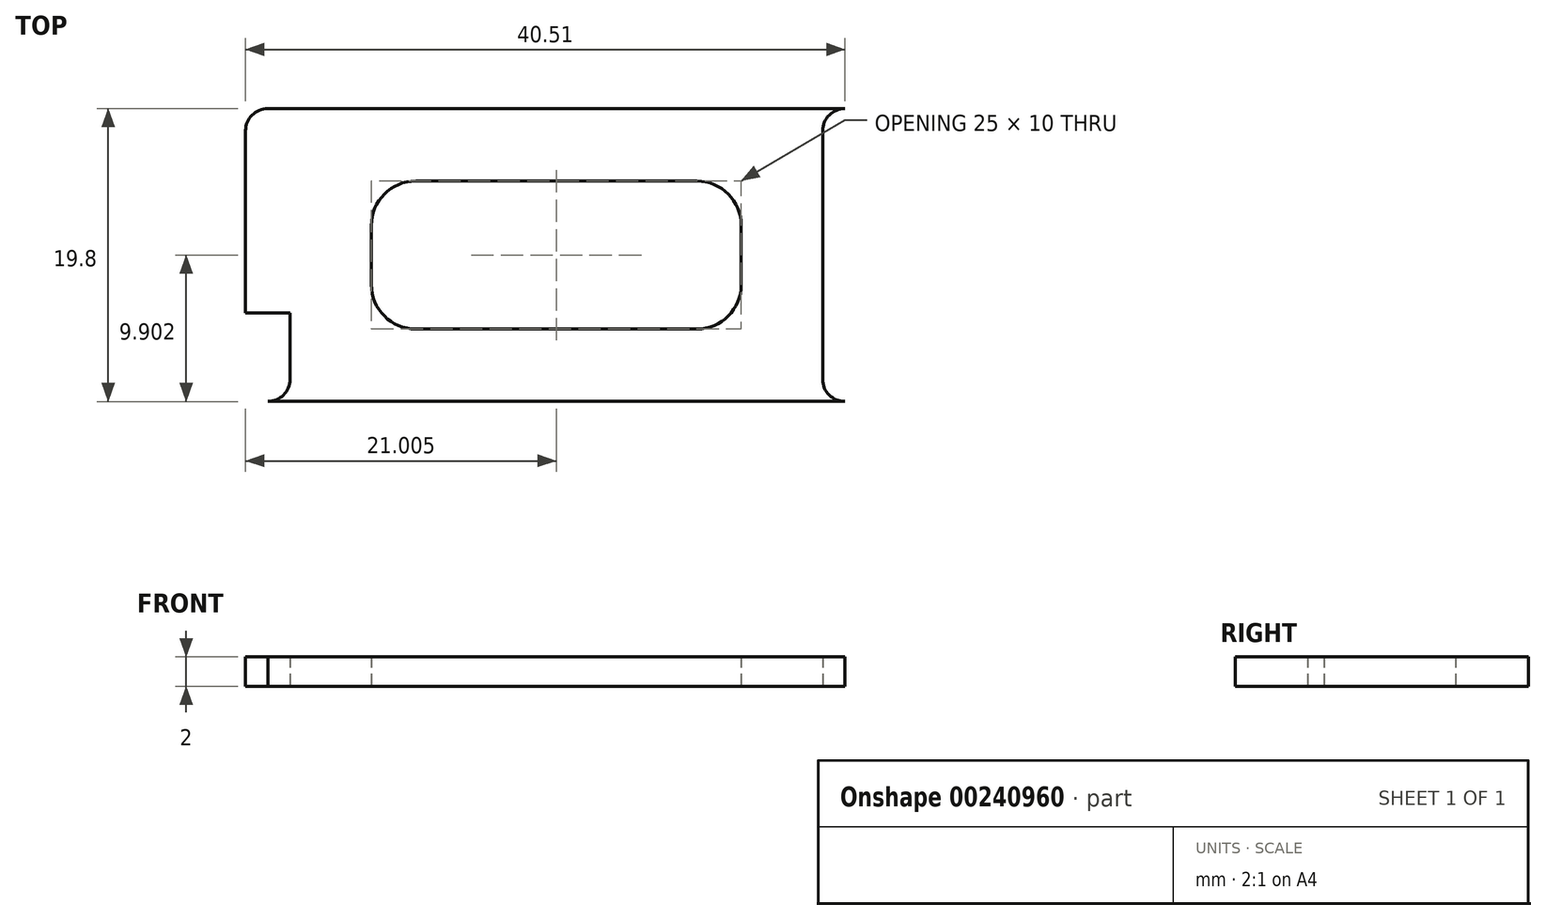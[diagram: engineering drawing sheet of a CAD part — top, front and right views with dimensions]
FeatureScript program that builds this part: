
annotation { "Feature Type Name" : "Feature", "Feature Type Description" : "" }
export const myFeature = defineFeature(function(context is Context, id is Id, definition is map)
    precondition{}
    {
        {
            var Q0;
            Q0=qCreatedBy(makeId("Top.planeOp"),FACE);
            var sketch = newSketch(context, id + "F0", { "sketchPlane" : qUnion([Q0])});
            skLineSegment(sketch, "E0.bottom", {"start": v(-18.53, 9.8) * mm, "end": v(-18.53, 9.8) * mm});
            skLineSegment(sketch, "E0.top", {"start": v(-18.53, -10) * mm, "end": v(-18.53, -10) * mm});
            skLineSegment(sketch, "E0.left", {"start": v(-20.03, 8.3) * mm, "end": v(-20.03, -8.5) * mm});
            skLineSegment(sketch, "E0.right", {"start": v(-17.03, 8.3) * mm, "end": v(-17.03, -8.5) * mm});
            skPoint(sketch, "E0.middle", {"position": v(-18.53, -0.1) * mm});
            skPoint(sketch, "E1.visualSharp", {"position": v(-20.03, 9.8) * mm});
            skArc(sketch, "E1.filletArc", {"start": v(-18.53, 9.8) * mm, "mid": v(-19.59, 9.35) * mm, "end": v(-20.03, 8.3) * mm});
            skPoint(sketch, "E2.visualSharp", {"position": v(-17.03, 9.8) * mm});
            skArc(sketch, "E2.filletArc", {"start": v(-17.03, 8.3) * mm, "mid": v(-17.46, 9.35) * mm, "end": v(-18.53, 9.8) * mm});
            skPoint(sketch, "E3.visualSharp", {"position": v(-17.03, -10) * mm});
            skArc(sketch, "E3.filletArc", {"start": v(-18.53, -10) * mm, "mid": v(-17.46, -9.57) * mm, "end": v(-17.03, -8.5) * mm});
            skPoint(sketch, "E4.visualSharp", {"position": v(-20.03, -10) * mm});
            skArc(sketch, "E4.filletArc", {"start": v(-20.03, -8.5) * mm, "mid": v(-19.59, -9.57) * mm, "end": v(-18.53, -10) * mm});
            skLineSegment(sketch, "E5", {"start": v(0.97, -11.31) * mm, "end": v(0.97, 19.7) * mm, "construction": true});
            skArc(sketch, "E6.MirrorCS", {"start": v(18.98, 8.3) * mm, "mid": v(19.41, 9.35) * mm, "end": v(20.48, 9.8) * mm});
            skArc(sketch, "E7.MirrorCS", {"start": v(20.48, -10) * mm, "mid": v(19.41, -9.57) * mm, "end": v(18.98, -8.5) * mm});
            skArc(sketch, "E8.MirrorCS", {"start": v(20.48, 9.8) * mm, "mid": v(21.54, 9.35) * mm, "end": v(21.98, 8.3) * mm});
            skArc(sketch, "E9.MirrorCS", {"start": v(21.98, -8.5) * mm, "mid": v(21.54, -9.57) * mm, "end": v(20.48, -10) * mm});
            skLineSegment(sketch, "E10.MirrorCS", {"start": v(18.97, 8.3) * mm, "end": v(18.97, -8.5) * mm});
            skLineSegment(sketch, "E11.MirrorCS", {"start": v(21.98, 8.3) * mm, "end": v(21.98, -8.5) * mm});
            skPoint(sketch, "E12.MirrorP", {"position": v(21.98, 9.8) * mm});
            skPoint(sketch, "E13.MirrorP", {"position": v(20.48, -0.1) * mm});
            skPoint(sketch, "E14.MirrorP", {"position": v(21.98, -10) * mm});
            skPoint(sketch, "E15.MirrorP", {"position": v(18.97, -10) * mm});
            skPoint(sketch, "E16.MirrorP", {"position": v(18.97, 9.8) * mm});
            skLineSegment(sketch, "E17", {"start": v(-18.53, 9.8) * mm, "end": v(20.48, 9.8) * mm});
            skLineSegment(sketch, "E18", {"start": v(-18.53, -10) * mm, "end": v(20.48, -10) * mm});
            skLineSegment(sketch, "E19.bottom", {"start": v(-8.53, 4.9) * mm, "end": v(10.47, 4.9) * mm});
            skLineSegment(sketch, "E19.top", {"start": v(-8.53, -5.1) * mm, "end": v(10.47, -5.1) * mm});
            skLineSegment(sketch, "E19.left", {"start": v(-11.53, 1.9) * mm, "end": v(-11.53, -2.1) * mm});
            skLineSegment(sketch, "E19.right", {"start": v(13.47, 1.9) * mm, "end": v(13.47, -2.1) * mm});
            skPoint(sketch, "E19.middle", {"position": v(0.97, -0.1) * mm});
            skPoint(sketch, "E20.visualSharp", {"position": v(-11.53, 4.9) * mm});
            skArc(sketch, "E20.filletArc", {"start": v(-8.53, 4.9) * mm, "mid": v(-10.65, 4.01) * mm, "end": v(-11.53, 1.9) * mm});
            skPoint(sketch, "E21.visualSharp", {"position": v(-11.53, -5.1) * mm});
            skArc(sketch, "E21.filletArc", {"start": v(-11.53, -2.1) * mm, "mid": v(-10.65, -4.23) * mm, "end": v(-8.53, -5.1) * mm});
            skPoint(sketch, "E22.visualSharp", {"position": v(13.47, -5.1) * mm});
            skArc(sketch, "E22.filletArc", {"start": v(10.47, -5.1) * mm, "mid": v(12.6, -4.23) * mm, "end": v(13.47, -2.1) * mm});
            skPoint(sketch, "E23.visualSharp", {"position": v(13.47, 4.9) * mm});
            skArc(sketch, "E23.filletArc", {"start": v(13.47, 1.9) * mm, "mid": v(12.6, 4.01) * mm, "end": v(10.47, 4.9) * mm});
            skLineSegment(sketch, "E24", {"start": v(-20.03, -4) * mm, "end": v(-17.03, -4) * mm});
            skLineSegment(sketch, "E25", {"start": v(18.97, 3.8) * mm, "end": v(21.97, 3.8) * mm});
            skSolve(sketch);
        }
        {
            var Q0;
            {var subQ1=sQuery(id+"F0.wireOp",EDGE,"E1.filletArc");Q0=makeQuery(id+"F0.imprint","IMPRINT",FACE,{"disambiguationData":[TD([[makeQuery(id+"F0.imprint","IMPRINT",EDGE,{"derivedFrom":subQ1}),1.0]])]});}
            var Q1;
            {var subQ2=sQuery(id+"F0.wireOp",EDGE,"E2.filletArc");Q1=makeQuery(id+"F0.imprint","IMPRINT",FACE,{"disambiguationData":[TD([[makeQuery(id+"F0.imprint","IMPRINT",EDGE,{"derivedFrom":subQ2}),-1.0]])]});}
            var Q2;
            {var subQ4=sQuery(id+"F0.wireOp",EDGE,"E7.MirrorCS");Q2=makeQuery(id+"F0.imprint","IMPRINT",FACE,{"disambiguationData":[TD([[makeQuery(id+"F0.imprint","IMPRINT",EDGE,{"derivedFrom":subQ4}),-1.0]])]});}
            extrude(context, id + "F1", {"entities" : qUnion([Q0, Q1, Q2]), "depth" : 2 * mm});
        }
    });
